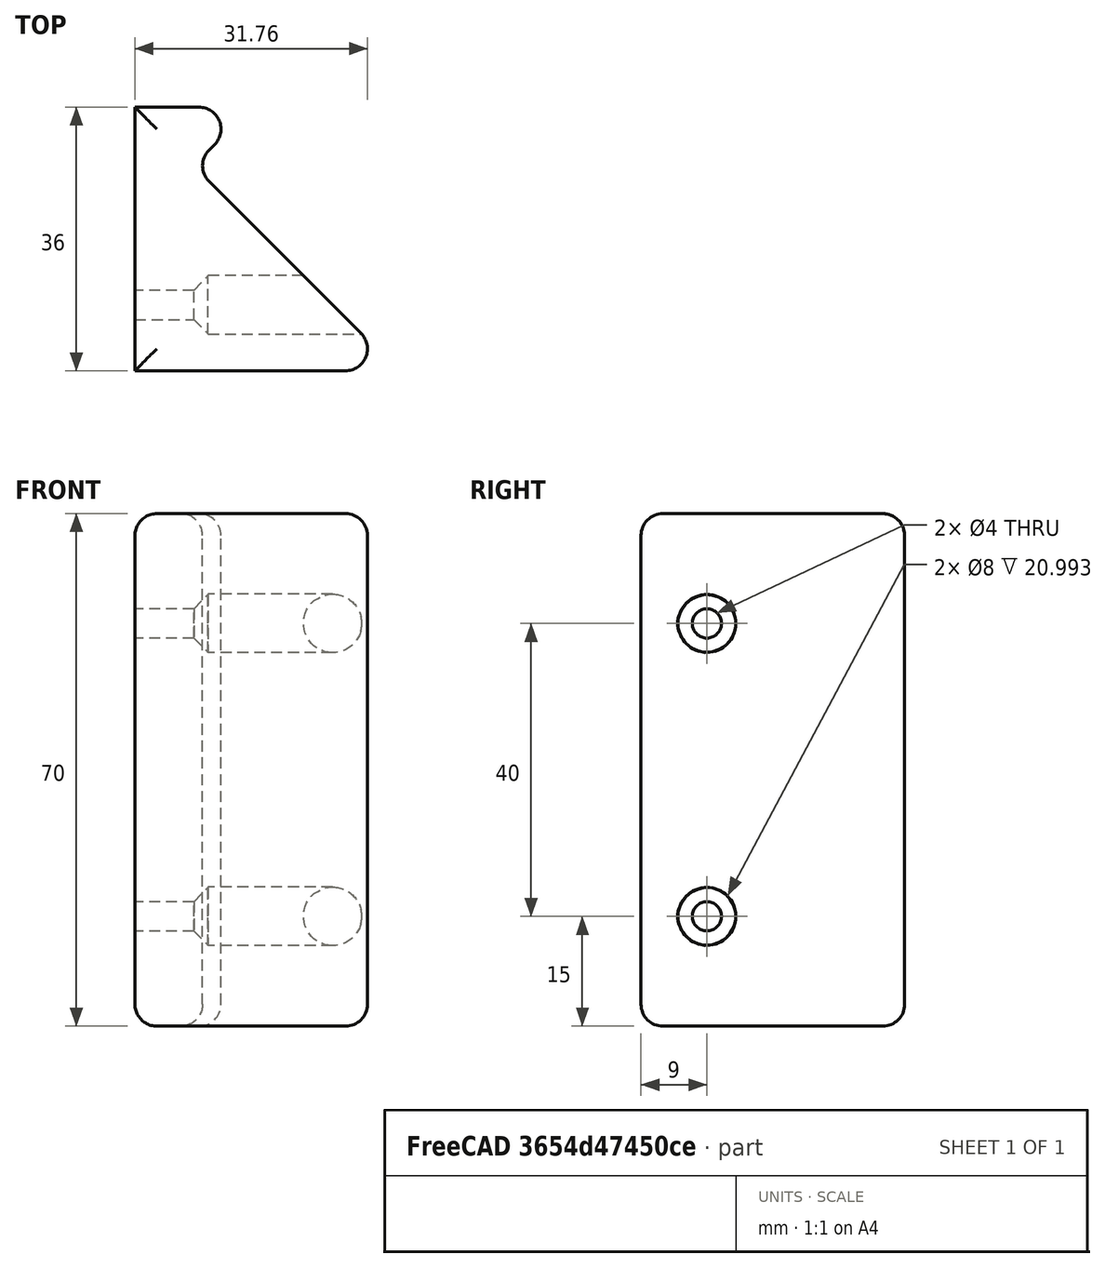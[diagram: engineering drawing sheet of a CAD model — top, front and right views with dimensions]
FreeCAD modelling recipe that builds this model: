
FCSTD DOCUMENT  (FreeCAD 0.20R)
Label: Poignée_V1
License: All rights reserved
LicenseURL: http://en.wikipedia.org/wiki/All_rights_reserved
objects: Sketcher::SketchObject×3, PartDesign::Pad×2, PartDesign::Fillet×1, PartDesign::Pocket×1, PartDesign::Chamfer×1, PartDesign::Body×1, Mesh::Feature×1
note: 14 computed .brp shape members not serialized (recipe doc carries the construction recipe); baked Part::Feature solids carry a one-line shape summary decoded from their .brp

FEATURE [Sketcher::SketchObject] Sketch
  FullyConstrained = true
  MapMode = 5
  Support = -> [XY_Plane]
  sketch-geometry (5):
    g0: LineSegment StartX=0 StartY=0 StartZ=0 EndX=0 EndY=36 EndZ=0
    g1: LineSegment StartX=0 StartY=36 StartZ=0 EndX=16 EndY=36 EndZ=0
    g2: LineSegment StartX=16 StartY=36 StartZ=0 EndX=8 EndY=28 EndZ=0
    g3: LineSegment StartX=8 StartY=28 StartZ=0 EndX=36 EndY=0 EndZ=0
    g4: LineSegment StartX=36 StartY=0 StartZ=0 EndX=0 EndY=0 EndZ=0
  constraints (14):
    c: Coincident(g-1,g0)
    c: PointOnObject(g0,g-2)
    c: Coincident(g0,g1)
    c: Horizontal(g1)
    c: Coincident(g1,g2)
    c: Coincident(g2,g3)
    c: PointOnObject(g3,g-1)
    c: Coincident(g3,g4)
    c: Coincident(g4,g0)
    c: DistanceX(g4,g4) = 36
    c: DistanceY(g0,g0) = 36
    c: Angle(g3,g4) = 0.785398
    c: Distance(g2,g0) = 8
    c: Perpendicular(g2,g3)
FEATURE [PartDesign::Pad] Pad
  Direction = (0,0,1)
  Length = 70
  Length2 = 100
  Profile = -> Sketch
  Type = 0
FEATURE [PartDesign::Fillet] Fillet
  Base = -> Pad [Face7,Face6,Edge5,Edge8,Edge11]
  BaseFeature = -> Pad
  Radius = 3
  SupportTransform = false
FEATURE [Sketcher::SketchObject] Sketch001
  ExternalGeometry = -> [Fillet]
  FullyConstrained = true
  MapMode = 5
  Placement = pos=(0,0,0) rot=(0.57735,-0.57735,-0.57735;2.0944rad)
  Support = -> [Fillet]
  sketch-geometry (2):
    g0: Circle CenterX=-9 CenterY=15 CenterZ=0 NormalX=0 NormalY=0 NormalZ=1 AngleXU=0 Radius=4
    g1: Circle CenterX=-9 CenterY=55 CenterZ=0 NormalX=0 NormalY=0 NormalZ=1 AngleXU=0 Radius=4
  constraints (6):
    c: DistanceX(g-2,g1) = -9
    c: DistanceX(g-2,g0) = -9
    c: Distance(g1,g-3) = 15
    c: DistanceY(g-1,g0) = 15
    c: Radius(g1) = 4
    c: Equal(g1,g0)
FEATURE [PartDesign::Pocket] Pocket
  BaseFeature = -> Fillet
  Length = 50
  Length2 = 100
  Profile = -> Sketch001
  Type = 0
FEATURE [Sketcher::SketchObject] Sketch002
  ExternalGeometry = -> [Pocket]
  FullyConstrained = true
  MapMode = 5
  Placement = pos=(0,0,0) rot=(0.57735,-0.57735,-0.57735;2.0944rad)
  Support = -> [Pocket]
  sketch-geometry (4):
    g0: Circle CenterX=-9 CenterY=15 CenterZ=0 NormalX=0 NormalY=0 NormalZ=1 AngleXU=0 Radius=2
    g1: Circle CenterX=-9 CenterY=55 CenterZ=0 NormalX=0 NormalY=0 NormalZ=1 AngleXU=0 Radius=2
    g2: Circle CenterX=-9 CenterY=55 CenterZ=0 NormalX=0 NormalY=0 NormalZ=1 AngleXU=0 Radius=6
    g3: Circle CenterX=-9 CenterY=15 CenterZ=0 NormalX=0 NormalY=0 NormalZ=1 AngleXU=0 Radius=6
  constraints (8):
    c: Coincident(g0,g-3)
    c: Coincident(g1,g-4)
    c: Coincident(g2,g1)
    c: Coincident(g3,g0)
    c: Radius(g3) = 6
    c: Equal(g3,g2)
    c: Radius(g0) = 2
    c: Equal(g0,g1)
FEATURE [PartDesign::Pad] Pad001
  BaseFeature = -> Pocket
  Direction = (-1,0,0)
  Length = 10
  Length2 = 100
  Profile = -> Sketch002
  Reversed = true
  Type = 0
FEATURE [PartDesign::Chamfer] Chamfer
  Angle = 45
  Base = -> Pad001 [Edge76,Edge78]
  BaseFeature = -> Pad001
  ChamferType = 0
  FlipDirection = false
  Size = 1.95
  Size2 = 1
  SupportTransform = false
FEATURE [PartDesign::Body] Body  label="Poignée"
  Group = -> [Sketch,Pad,Fillet,Sketch001,Pocket,Sketch002,Pad001,Chamfer]
  Origin = -> Origin
  Tip = -> Chamfer
FEATURE [Mesh::Feature] Mesh  label="Poignée (Meshed)"
